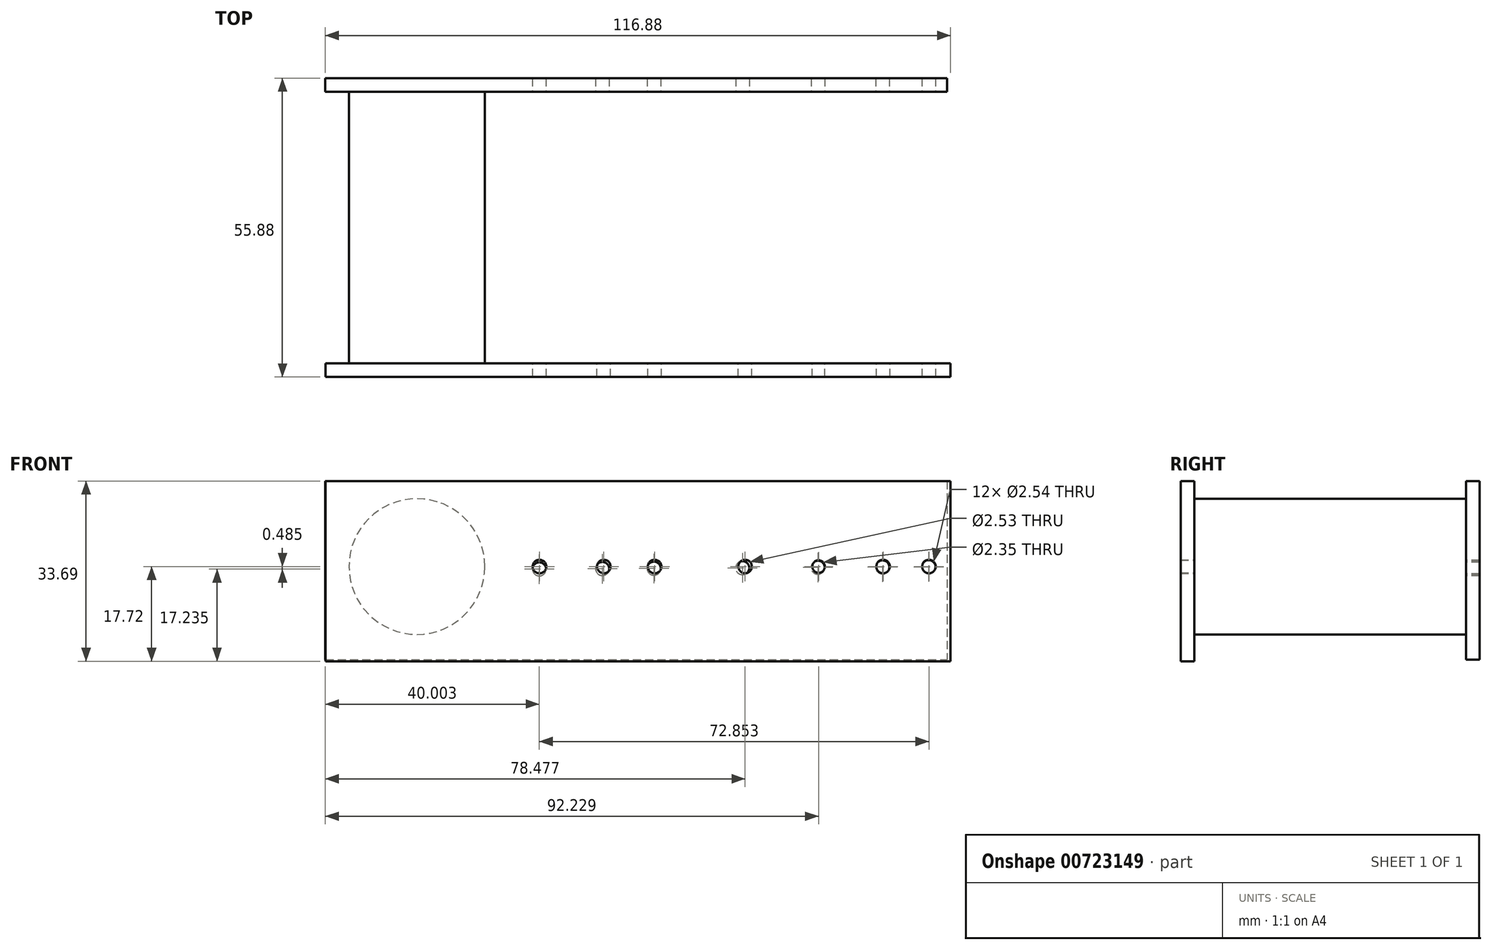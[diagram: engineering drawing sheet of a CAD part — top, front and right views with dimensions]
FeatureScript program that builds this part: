
annotation { "Feature Type Name" : "Feature", "Feature Type Description" : "" }
export const myFeature = defineFeature(function(context is Context, id is Id, definition is map)
    precondition{}
    {
        {
            var Q0;
            Q0=qCreatedBy(makeId("Front.planeOp"),FACE);
            var sketch = newSketch(context, id + "F0", { "sketchPlane" : qUnion([Q0])});
            skCircle(sketch, "E0", {"center": v(0, 0) * mm, "radius": 12.7 * mm});
            skPoint(sketch, "E1.start.orphan", {"position": v(0, 12.7) * mm});
            skPoint(sketch, "E2.start.orphan", {"position": v(-50.8, 0) * mm});
            skPoint(sketch, "E3.end.orphan", {"position": v(0, -12.7) * mm});
            skSolve(sketch);
        }
        {
            var Q0;
            Q0=makeQuery(id+"F0.imprint","IMPRINT",FACE,{"disambiguationData":[TD([[makeQuery(id+"F0.imprint","IMPRINT",EDGE,{"derivedFrom":sQuery(id+"F0.wireOp",EDGE,"E0")}),1.0]])]});
            extrude(context, id + "F1", {"entities" : qUnion([Q0]), "depth" : 50.8 * mm, "offsetDistance" : 25.4 * mm});
        }
        {
            var Q0;
            Q0=makeQuery(id+"F1.opExtrude","CAP_FACE",FACE,{"disambiguationData":[OSD([sQuery(id+"F0.wireOp",EDGE,"E0")])],"isStart":false});
            var sketch = newSketch(context, id + "F2", { "sketchPlane" : qUnion([Q0])});
            skCircle(sketch, "E4", {"center": v(0, 0) * mm, "radius": 1.27 * mm});
            skSolve(sketch);
        }
        {
            var Q0;
            Q0 = qSketchRegion(id + "F2", true);
            extrude(context, id + "F3", {"entities" : qUnion([Q0]), "operationType" : NewBodyOperationType.ADD, "depth" : 2.54 * mm, "offsetDistance" : 25.4 * mm});
        }
        {
            var Q0;
            Q0=makeQuery(id+"F1.opExtrude","CAP_FACE",FACE,{"disambiguationData":[OSD([sQuery(id+"F0.wireOp",EDGE,"E0")])],"isStart":true});
            var sketch = newSketch(context, id + "F4", { "sketchPlane" : qUnion([Q0])});
            skCircle(sketch, "E5", {"center": v(0, 0) * mm, "radius": 1.27 * mm});
            skSolve(sketch);
        }
        {
            var Q0;
            Q0=makeQuery(id+"F4.imprint","IMPRINT",FACE,{"disambiguationData":[TD([[makeQuery(id+"F4.imprint","IMPRINT",EDGE,{"derivedFrom":sQuery(id+"F4.wireOp",EDGE,"E5")}),1.0]])]});
            extrude(context, id + "F5", {"entities" : qUnion([Q0]), "operationType" : NewBodyOperationType.ADD, "depth" : 2.54 * mm, "offsetDistance" : 25.4 * mm});
        }
        {
            var Q0;
            Q0=qCreatedBy(makeId("Front.planeOp"),FACE);
            var sketch = newSketch(context, id + "F6", { "sketchPlane" : qUnion([Q0])});
            skLineSegment(sketch, "E6.bottom", {"start": v(-17.12, 15.97) * mm, "end": v(99.15, 15.97) * mm});
            skLineSegment(sketch, "E6.top", {"start": v(-17.12, -17.41) * mm, "end": v(99.15, -17.41) * mm});
            skLineSegment(sketch, "E6.left", {"start": v(-17.12, 15.97) * mm, "end": v(-17.12, -17.41) * mm});
            skLineSegment(sketch, "E6.right", {"start": v(99.15, 15.97) * mm, "end": v(99.15, -17.41) * mm});
            skLineSegment(sketch, "E7", {"start": v(-17.12, -0.72) * mm, "end": v(105.77, 0) * mm});
            skCircle(sketch, "E8", {"center": v(22.88, -0.49) * mm, "radius": 1.27 * mm});
            skCircle(sketch, "E9", {"center": v(34.68, -0.42) * mm, "radius": 1.27 * mm});
            skCircle(sketch, "E10", {"center": v(44.32, -0.36) * mm, "radius": 1.27 * mm});
            skCircle(sketch, "E11", {"center": v(60.87, -0.26) * mm, "radius": 1.27 * mm});
            skCircle(sketch, "E12", {"center": v(74.98, -0.18) * mm, "radius": 1.27 * mm});
            skCircle(sketch, "E13", {"center": v(87.06, -0.1) * mm, "radius": 1.27 * mm});
            skCircle(sketch, "E14", {"center": v(95.7, -0.06) * mm, "radius": 1.27 * mm});
            skSolve(sketch);
        }
        {
            var Q0;
            {var subQ15=sQuery(id+"F6.wireOp",EDGE,"E6.top");Q0=makeQuery(id+"F6.imprint","IMPRINT",FACE,{"disambiguationData":[TD([[makeQuery(id+"F6.imprint","IMPRINT",EDGE,{"derivedFrom":subQ15}),1.0]])]});}
            var Q1;
            {var subQ21=sQuery(id+"F6.wireOp",EDGE,"E6.bottom");Q1=makeQuery(id+"F6.imprint","IMPRINT",FACE,{"disambiguationData":[TD([[makeQuery(id+"F6.imprint","IMPRINT",EDGE,{"derivedFrom":subQ21}),-1.0]])]});}
            extrude(context, id + "F7", {"entities" : qUnion([Q0, Q1]), "operationType" : NewBodyOperationType.ADD, "oppositeDirection" : true, "depth" : 2.54 * mm, "offsetDistance" : 25.4 * mm});
        }
        {
            var Q0;
            Q0=makeQuery(id+"F1.opExtrude","CAP_FACE",FACE,{"disambiguationData":[OSD([sQuery(id+"F0.wireOp",EDGE,"E0")])],"isStart":false});
            var sketch = newSketch(context, id + "F8", { "sketchPlane" : qUnion([Q0])});
            skLineSegment(sketch, "E15.bottom", {"start": v(-17.09, 15.95) * mm, "end": v(99.76, 15.95) * mm});
            skLineSegment(sketch, "E15.top", {"start": v(-17.09, -17.72) * mm, "end": v(99.76, -17.72) * mm});
            skLineSegment(sketch, "E15.left", {"start": v(-17.09, 15.95) * mm, "end": v(-17.09, -17.72) * mm});
            skLineSegment(sketch, "E15.right", {"start": v(99.76, 15.95) * mm, "end": v(99.76, -17.72) * mm});
            skCircle(sketch, "E16", {"center": v(0, 0) * mm, "radius": 1.27 * mm});
            skCircle(sketch, "E17", {"center": v(22.92, 0) * mm, "radius": 1.27 * mm});
            skCircle(sketch, "E18", {"center": v(34.95, 0) * mm, "radius": 1.27 * mm});
            skCircle(sketch, "E19", {"center": v(44.45, 0) * mm, "radius": 1.27 * mm});
            skCircle(sketch, "E20", {"center": v(61.36, 0) * mm, "radius": 1.27 * mm});
            skCircle(sketch, "E21", {"center": v(75.1, 0) * mm, "radius": 1.17 * mm});
            skCircle(sketch, "E22", {"center": v(87.16, 0) * mm, "radius": 1.27 * mm});
            skCircle(sketch, "E23", {"center": v(95.74, 0) * mm, "radius": 1.27 * mm});
            skSolve(sketch);
        }
        {
            var Q0;
            Q0 = qSketchRegion(id + "F8", true);
            extrude(context, id + "F9", {"entities" : qUnion([Q0]), "operationType" : NewBodyOperationType.ADD, "depth" : 2.54 * mm, "offsetDistance" : 25.4 * mm});
        }
    });
